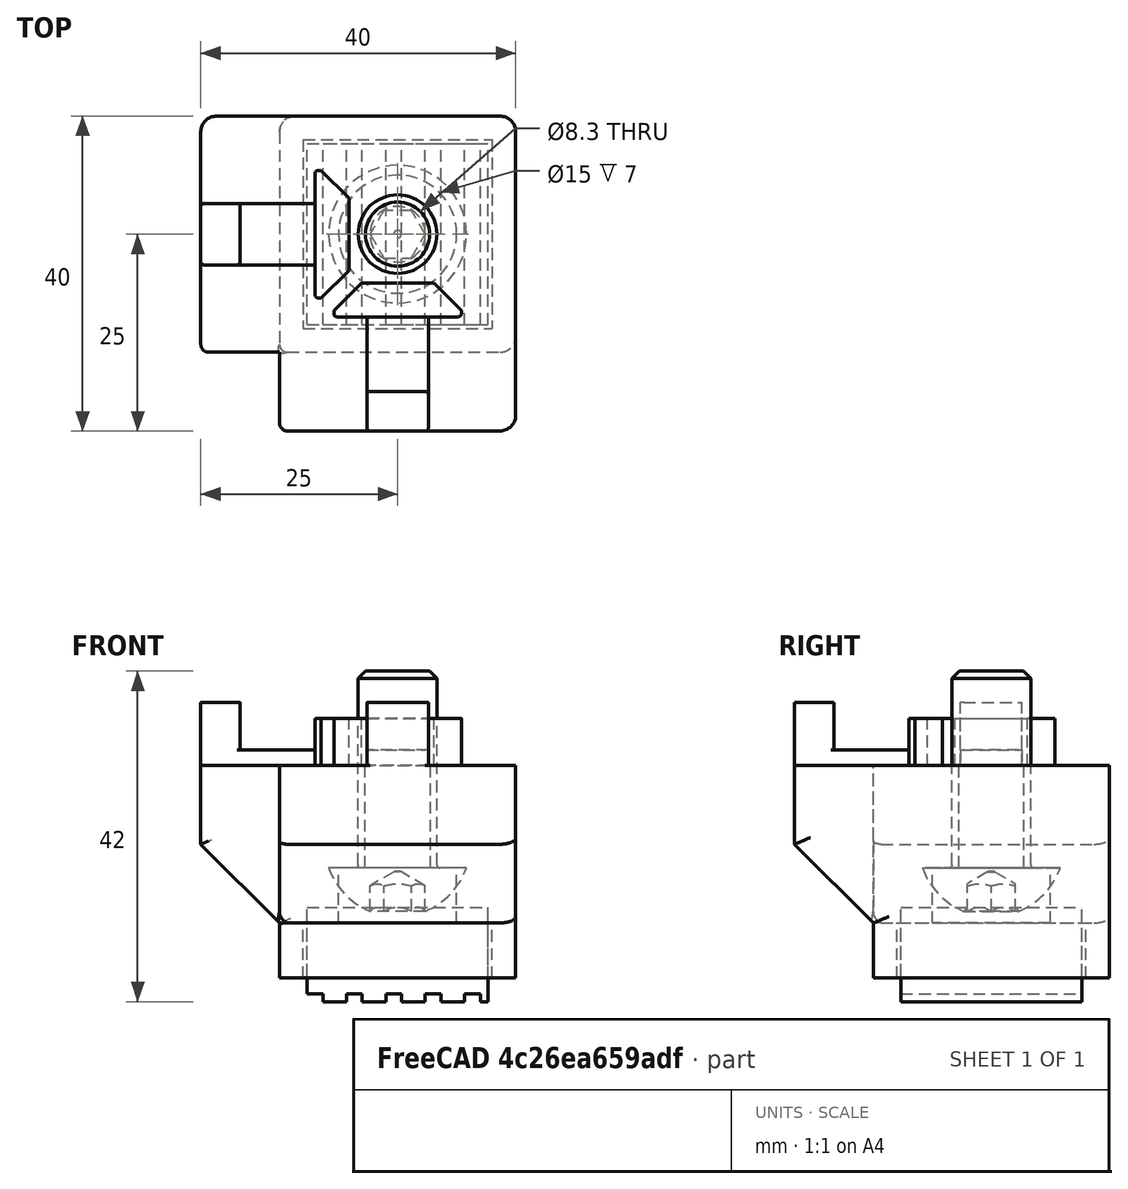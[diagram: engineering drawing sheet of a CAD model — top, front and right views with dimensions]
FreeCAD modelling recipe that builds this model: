
FCSTD DOCUMENT  (FreeCAD 0.19R24291 (Git))
Label: foot-single-assembly
License: Other
LicenseURL: GPL3
objects: Part::Feature×2, Spreadsheet::Sheet×2, PartDesign::CoordinateSystem×1, Part::FeaturePython×1, App::Part×1
note: 4 computed .brp shape members not serialized (recipe doc carries the construction recipe); baked Part::Feature solids carry a one-line shape summary decoded from their .brp

FEATURE [Part::Feature] Cut002002001001  label="subber"
  shape: bbox 23 x 23 x 12 mm, 24 faces (baked)
FEATURE [Part::Feature] Cut002003001001  label="foot-corner"
  shape: bbox 40.3 x 40.3 x 35.3 mm, 68 faces (baked)
FEATURE [PartDesign::CoordinateSystem] LCS_foot
  AttacherType = Attacher::AttachEngine3D
FEATURE [Part::FeaturePython] Screw  label="M10x25-Screw"  # Fasteners workbench fastener (typed FeaturePython)
  Placement = pos=(0,0,17) rot=(1,0,0;3.14159rad)
  baseObject = -> Cut002003001001 [Edge127]
  diameter = 6
  invert = true
  length = 2
  lengthCustom = 25
  matchOuter = false
  offset = 0
  thread = false
  type = 40
FEATURE [App::Part] Part  label="foot"
  Group = -> [Cut002003001001,Cut002002001001,LCS_foot,Screw]
  Origin = -> Origin
FEATURE [Spreadsheet::Sheet] Fasteners_BOM
  cells = A1=Type; B1=Qty; A2=ISO7380-1 Screw M10x25; B2=5
FEATURE [Spreadsheet::Sheet] Fasteners_BOM001
  cells = A1=Type; B1=Qty; A2=ISO7380-1 Screw M10x25; B2=5
